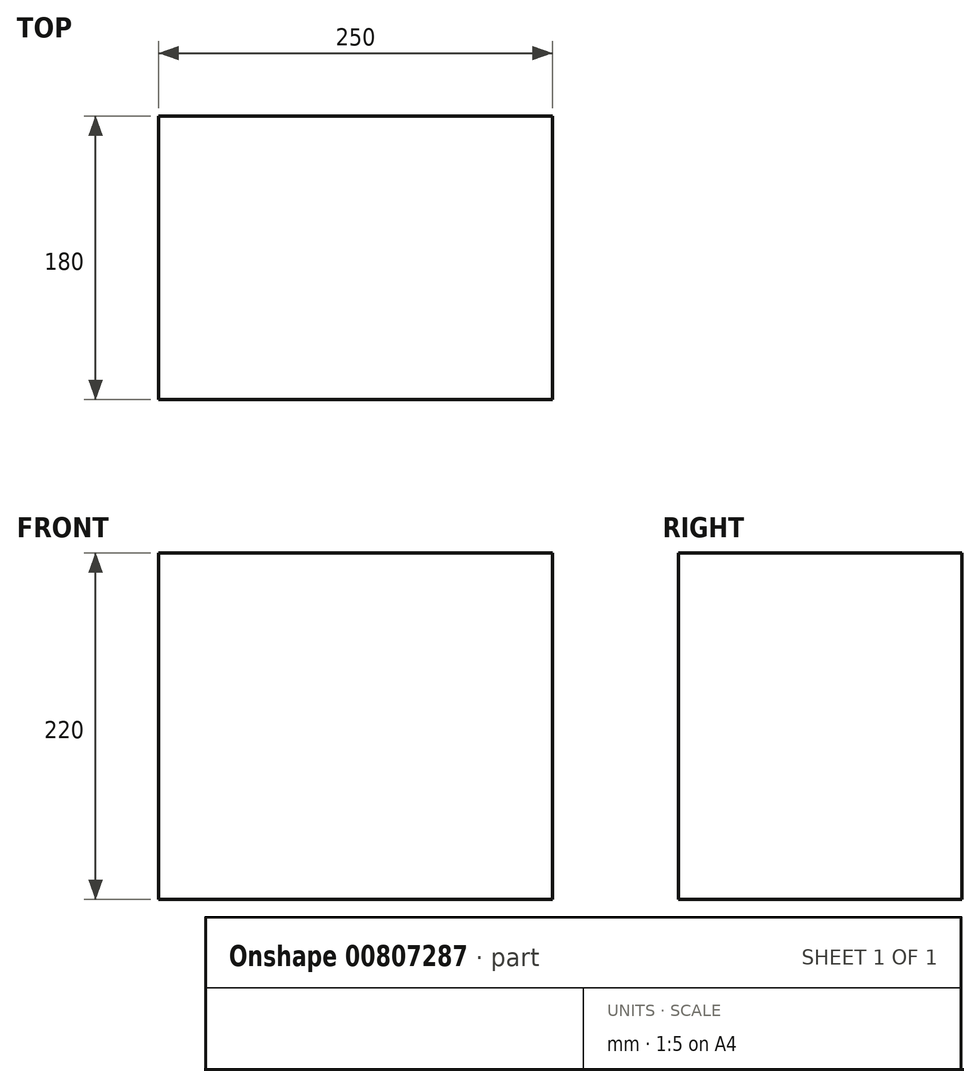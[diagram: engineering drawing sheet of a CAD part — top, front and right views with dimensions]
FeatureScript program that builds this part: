
annotation { "Feature Type Name" : "Feature", "Feature Type Description" : "" }
export const myFeature = defineFeature(function(context is Context, id is Id, definition is map)
    precondition{}
    {
        {
            var Q0;
            Q0=qCreatedBy(makeId("Top.planeOp"),FACE);
            var sketch = newSketch(context, id + "F0", { "sketchPlane" : qUnion([Q0])});
            skLineSegment(sketch, "E0.bottom", {"start": v(-12320.69, 2113.8) * mm, "end": v(-12070.69, 2113.8) * mm});
            skLineSegment(sketch, "E0.top", {"start": v(-12320.69, 1933.8) * mm, "end": v(-12070.69, 1933.8) * mm});
            skLineSegment(sketch, "E0.left", {"start": v(-12320.69, 2113.8) * mm, "end": v(-12320.69, 1933.8) * mm});
            skLineSegment(sketch, "E0.right", {"start": v(-12070.69, 2113.8) * mm, "end": v(-12070.69, 1933.8) * mm});
            skSolve(sketch);
        }
        {
            var Q0;
            Q0 = qSketchRegion(id + "F0", true);
            extrude(context, id + "F1", {"entities" : qUnion([Q0]), "depth" : 220 * mm, "offsetDistance" : 25 * mm});
        }
    });
